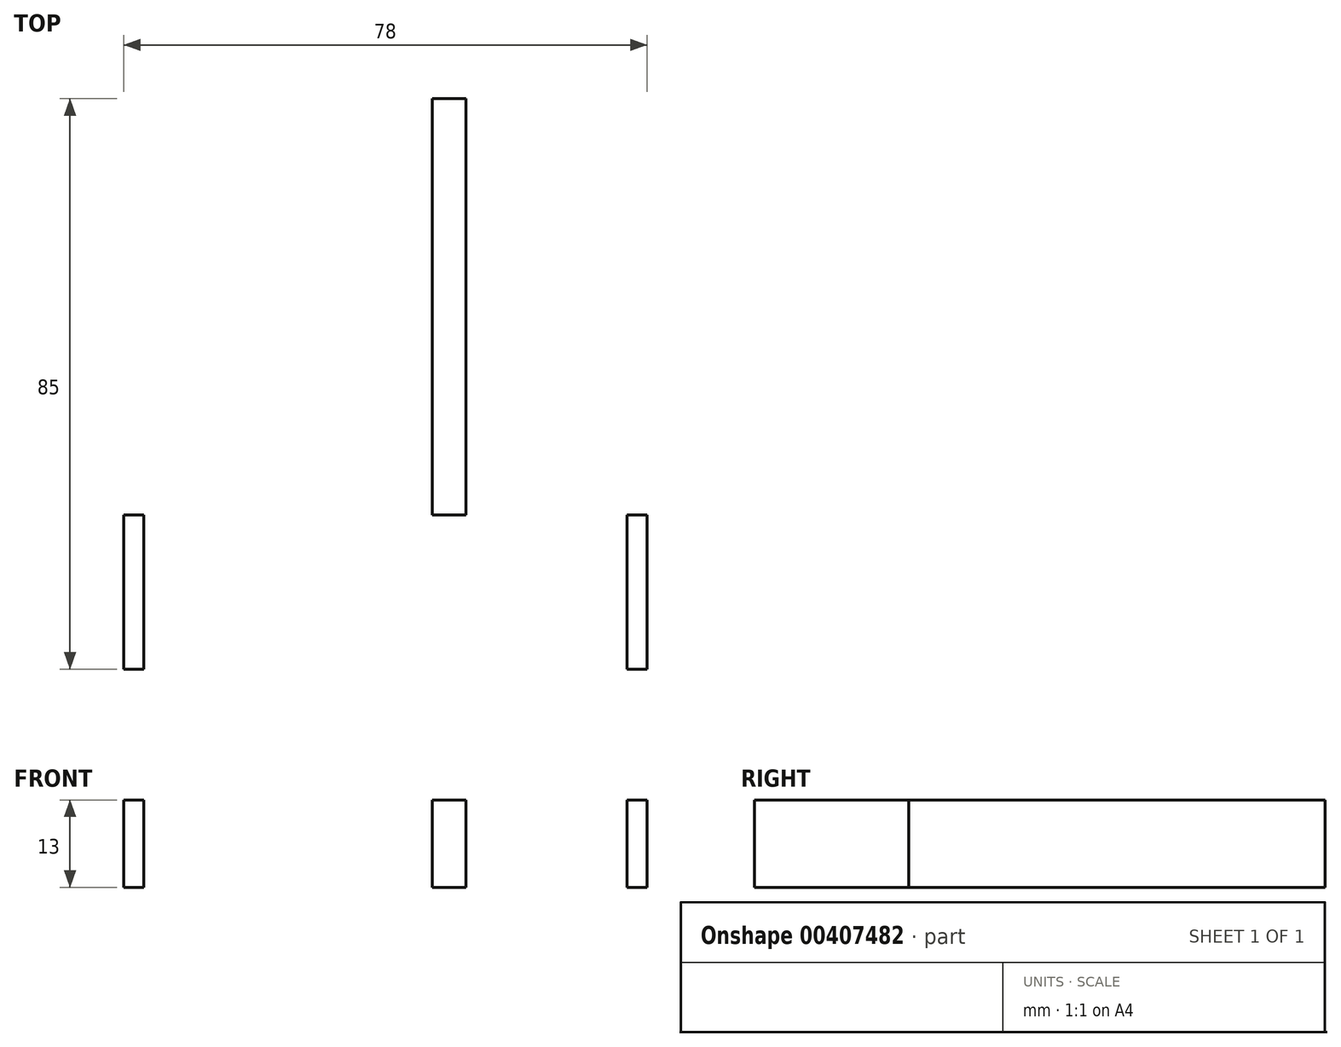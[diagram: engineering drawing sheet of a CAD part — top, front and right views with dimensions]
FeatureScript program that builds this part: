
annotation { "Feature Type Name" : "Feature", "Feature Type Description" : "" }
export const myFeature = defineFeature(function(context is Context, id is Id, definition is map)
    precondition{}
    {
        {
            var Q0;
            Q0=qCreatedBy(makeId("Top.planeOp"),FACE);
            var sketch = newSketch(context, id + "F0", { "sketchPlane" : qUnion([Q0])});
            skLineSegment(sketch, "E0.bottom", {"start": v(-36, 0) * mm, "end": v(36, 0) * mm});
            skLineSegment(sketch, "E0.top", {"start": v(-36, 3) * mm, "end": v(36, 3) * mm});
            skLineSegment(sketch, "E0.left", {"start": v(-36, 0) * mm, "end": v(-36, 3) * mm});
            skLineSegment(sketch, "E0.right", {"start": v(36, 0) * mm, "end": v(36, 3) * mm});
            skLineSegment(sketch, "E1.bottom", {"start": v(-36, 3) * mm, "end": v(-39, 3) * mm});
            skLineSegment(sketch, "E1.top", {"start": v(-36, -20) * mm, "end": v(-39, -20) * mm});
            skLineSegment(sketch, "E1.left", {"start": v(-36, 3) * mm, "end": v(-36, -20) * mm});
            skLineSegment(sketch, "E1.right", {"start": v(-39, 3) * mm, "end": v(-39, -20) * mm});
            skLineSegment(sketch, "E2.MirrorCS", {"start": v(36, -20) * mm, "end": v(39, -20) * mm});
            skLineSegment(sketch, "E3.MirrorCS", {"start": v(36, 3) * mm, "end": v(39, 3) * mm});
            skLineSegment(sketch, "E4.MirrorCS", {"start": v(36, 0) * mm, "end": v(-36, 0) * mm});
            skLineSegment(sketch, "E5.MirrorCS", {"start": v(36, 3) * mm, "end": v(-36, 3) * mm});
            skLineSegment(sketch, "E6.MirrorCS", {"start": v(39, 3) * mm, "end": v(39, -20) * mm});
            skLineSegment(sketch, "E7.MirrorCS", {"start": v(36, 3) * mm, "end": v(36, -20) * mm});
            skPoint(sketch, "E8", {"position": v(-7, 3) * mm});
            skPoint(sketch, "E9.MirrorP", {"position": v(7, 3) * mm});
            skLineSegment(sketch, "E10.bottom", {"start": v(-7, 3) * mm, "end": v(-12, 3) * mm});
            skLineSegment(sketch, "E10.top", {"start": v(-7, 65) * mm, "end": v(-12, 65) * mm});
            skLineSegment(sketch, "E10.left", {"start": v(-7, 3) * mm, "end": v(-7, 65) * mm});
            skLineSegment(sketch, "E10.right", {"start": v(-12, 3) * mm, "end": v(-12, 65) * mm});
            skLineSegment(sketch, "E11.MirrorCS", {"start": v(7, 3) * mm, "end": v(7, 65) * mm});
            skLineSegment(sketch, "E12.MirrorCS", {"start": v(7, 65) * mm, "end": v(12, 65) * mm});
            skLineSegment(sketch, "E13.MirrorCS", {"start": v(12, 3) * mm, "end": v(12, 65) * mm});
            skLineSegment(sketch, "E14.MirrorCS", {"start": v(7, 3) * mm, "end": v(12, 3) * mm});
            skSolve(sketch);
        }
        {
            var Q0;
            {var subQ3=sQuery(id+"F0.wireOp",EDGE,"E2.MirrorCS");Q0=makeQuery(id+"F0.imprint","IMPRINT",FACE,{"disambiguationData":[TD([[makeQuery(id+"F0.imprint","IMPRINT",EDGE,{"derivedFrom":subQ3}),1.0]])]});}
            var Q1;
            Q1=makeQuery(id+"F0.imprint","IMPRINT",FACE,{"disambiguationData":[TD([[makeQuery(id+"F0.imprint","IMPRINT",EDGE,{"derivedFrom":sQuery(id+"F0.wireOp",EDGE,"E10.bottom")}),-1.0]])]});
            var Q2;
            Q2=makeQuery(id+"F0.imprint","IMPRINT",FACE,{"disambiguationData":[TD([[makeQuery(id+"F0.imprint","IMPRINT",EDGE,{"derivedFrom":sQuery(id+"F0.wireOp",EDGE,"E12.MirrorCS")}),-1.0]])]});
            var Q3;
            {var subQ5=sQuery(id+"F0.wireOp",EDGE,"E4.MirrorCS");Q3=makeQuery(id+"F0.imprint","IMPRINT",FACE,{"disambiguationData":[TD([[makeQuery(id+"F0.imprint","IMPRINT",EDGE,{"derivedFrom":subQ5}),-1.0]])]});}
            var Q4;
            {var subQ3=sQuery(id+"F0.wireOp",EDGE,"E1.bottom");Q4=makeQuery(id+"F0.imprint","IMPRINT",FACE,{"disambiguationData":[TD([[makeQuery(id+"F0.imprint","IMPRINT",EDGE,{"derivedFrom":subQ3}),1.0]])]});}
            extrude(context, id + "F1", {"entities" : qUnion([Q0, Q1, Q2, Q3, Q4]), "depth" : 13 * mm});
        }
    });
